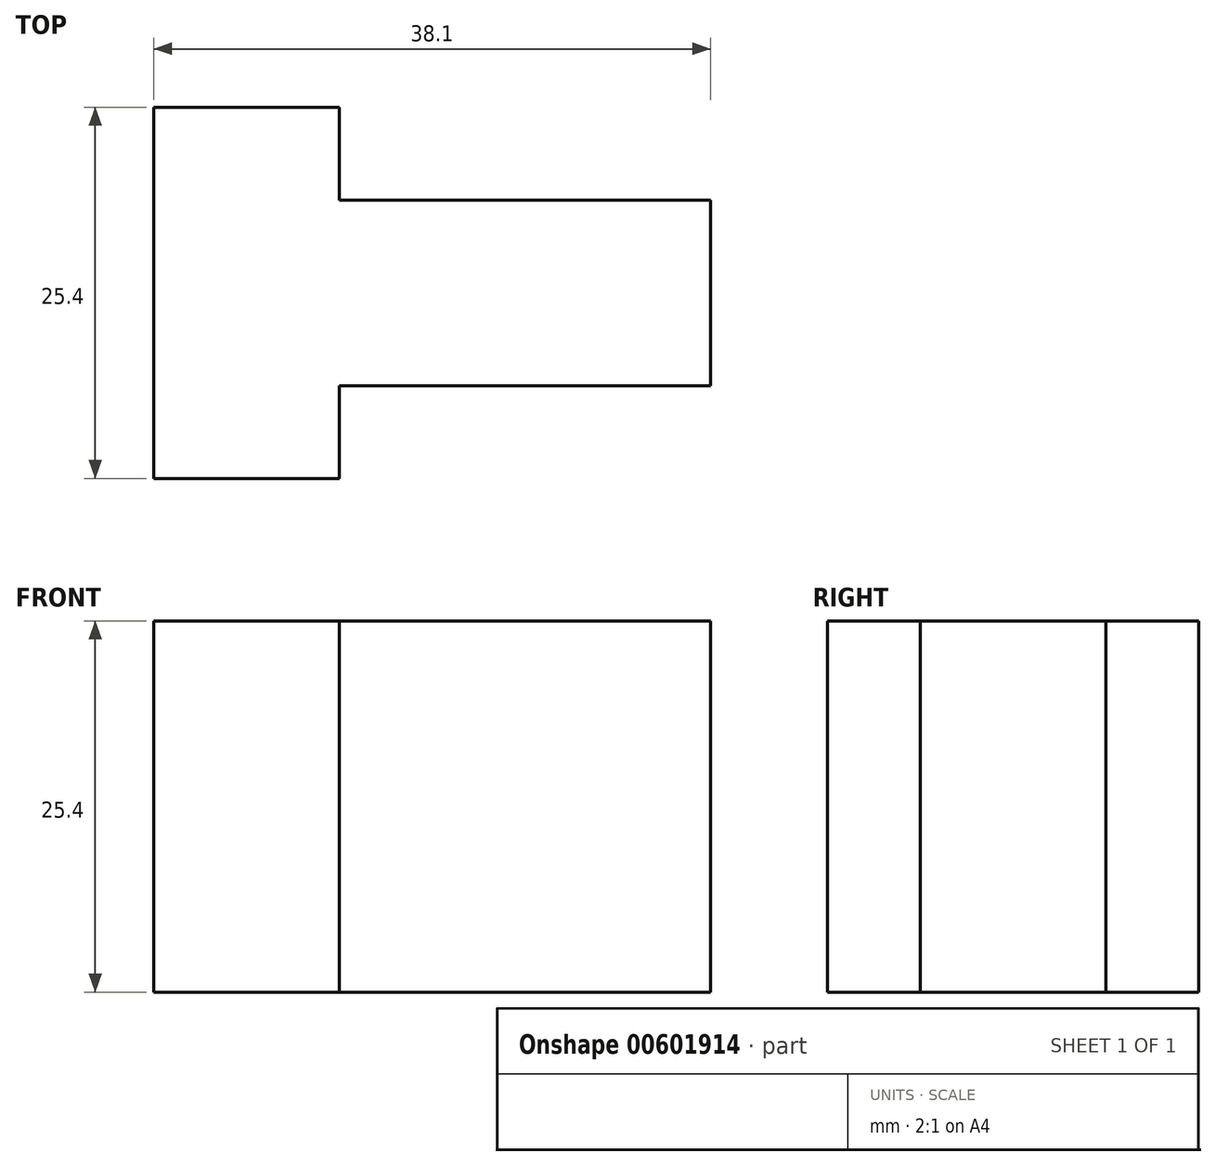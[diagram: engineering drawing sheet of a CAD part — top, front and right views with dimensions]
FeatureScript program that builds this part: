
annotation { "Feature Type Name" : "Feature", "Feature Type Description" : "" }
export const myFeature = defineFeature(function(context is Context, id is Id, definition is map)
    precondition{}
    {
        {
            var Q0;
            Q0=qCreatedBy(makeId("Top.planeOp"),FACE);
            var sketch = newSketch(context, id + "F0", { "sketchPlane" : qUnion([Q0])});
            skLineSegment(sketch, "E0", {"start": v(0, 0) * mm, "end": v(0, 25.4) * mm});
            skLineSegment(sketch, "E1", {"start": v(0, 25.4) * mm, "end": v(12.7, 25.4) * mm});
            skLineSegment(sketch, "E2", {"start": v(12.7, 25.4) * mm, "end": v(12.7, 19.05) * mm});
            skLineSegment(sketch, "E3", {"start": v(12.7, 19.05) * mm, "end": v(38.1, 19.05) * mm});
            skLineSegment(sketch, "E4", {"start": v(38.1, 19.05) * mm, "end": v(38.1, 6.35) * mm});
            skLineSegment(sketch, "E5", {"start": v(38.1, 6.35) * mm, "end": v(12.7, 6.35) * mm});
            skLineSegment(sketch, "E6", {"start": v(12.7, 6.35) * mm, "end": v(12.7, 0) * mm});
            skLineSegment(sketch, "E7", {"start": v(12.7, 0) * mm, "end": v(0, 0) * mm});
            skSolve(sketch);
        }
        {
            var Q0;
            Q0=makeQuery(id+"F0.imprint","IMPRINT",FACE,{"disambiguationData":[TD([[makeQuery(id+"F0.imprint","IMPRINT",EDGE,{"derivedFrom":sQuery(id+"F0.wireOp",EDGE,"E0")}),-1.0]])]});
            extrude(context, id + "F1", {"entities" : qUnion([Q0]), "depth" : 25.4 * mm, "offsetDistance" : 25.4 * mm});
        }
    });
